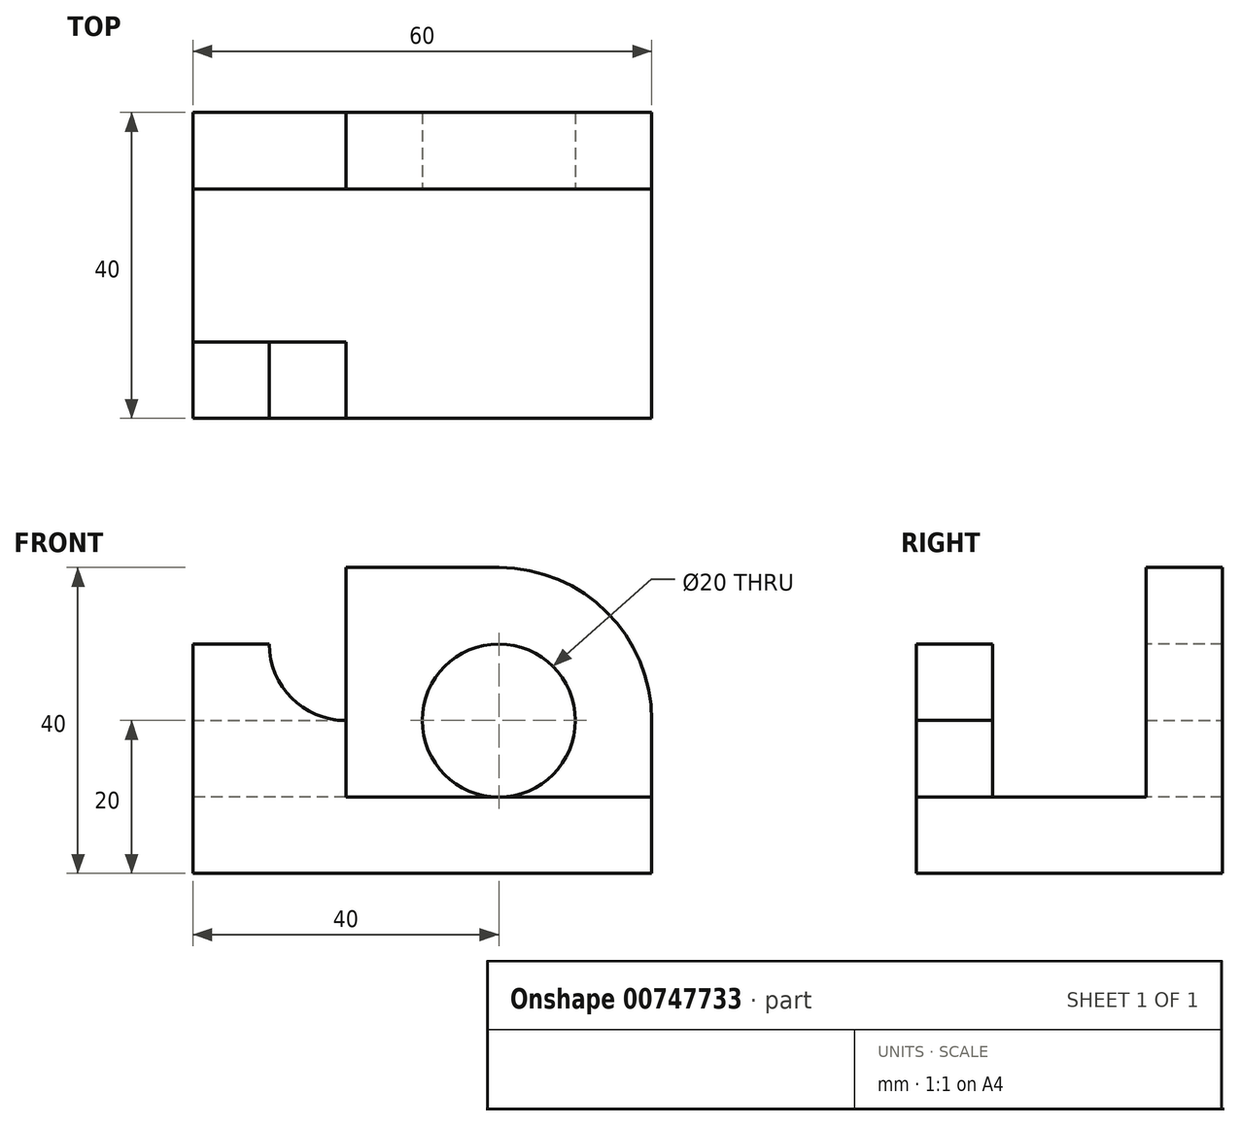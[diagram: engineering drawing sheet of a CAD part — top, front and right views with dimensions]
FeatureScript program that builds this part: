
annotation { "Feature Type Name" : "Feature", "Feature Type Description" : "" }
export const myFeature = defineFeature(function(context is Context, id is Id, definition is map)
    precondition{}
    {
        {
            var Q0;
            Q0=qCreatedBy(makeId("Top.planeOp"),FACE);
            var sketch = newSketch(context, id + "F0", { "sketchPlane" : qUnion([Q0])});
            skLineSegment(sketch, "E0", {"start": v(0, 0) * mm, "end": v(60, 0) * mm});
            skLineSegment(sketch, "E1", {"start": v(60, 0) * mm, "end": v(60, 40) * mm});
            skLineSegment(sketch, "E2", {"start": v(60, 40) * mm, "end": v(0, 40) * mm});
            skLineSegment(sketch, "E3", {"start": v(0, 40) * mm, "end": v(0, 0) * mm});
            skSolve(sketch);
        }
        {
            var Q0;
            Q0=qSketchRegion(id+"F0",true);
            extrude(context, id + "F1", {"entities" : qUnion([Q0]), "depth" : 40 * mm, "offsetDistance" : 25 * mm});
        }
        {
            var Q0;
            Q0=makeQuery(id+"F1.opExtrude","CAP_FACE",FACE,{"disambiguationData":[OSD([sQuery(id+"F0.wireOp",EDGE,"E0"),sQuery(id+"F0.wireOp",EDGE,"E1"),sQuery(id+"F0.wireOp",EDGE,"E2"),sQuery(id+"F0.wireOp",EDGE,"E3")])],"isStart":false});
            var sketch = newSketch(context, id + "F2", { "sketchPlane" : qUnion([Q0])});
            skLineSegment(sketch, "E4", {"start": v(0, 40) * mm, "end": v(0, 30) * mm});
            skLineSegment(sketch, "E5", {"start": v(0, 30) * mm, "end": v(0, 10) * mm});
            skLineSegment(sketch, "E6", {"start": v(0, 10) * mm, "end": v(60, 10) * mm});
            skLineSegment(sketch, "E7", {"start": v(60, 10) * mm, "end": v(60, 30) * mm});
            skLineSegment(sketch, "E8", {"start": v(60, 30) * mm, "end": v(0, 30) * mm});
            skLineSegment(sketch, "E9", {"start": v(0, 40) * mm, "end": v(20, 40) * mm});
            skLineSegment(sketch, "E10", {"start": v(20, 40) * mm, "end": v(20, 30) * mm});
            skLineSegment(sketch, "E11", {"start": v(20, 30) * mm, "end": v(0, 30) * mm});
            skSolve(sketch);
        }
        {
            var Q0;
            Q0=makeQuery(id+"F2.imprint","IMPRINT",FACE,{"disambiguationData":[TD([[makeQuery(id+"F2.imprint","IMPRINT",EDGE,{"derivedFrom":sQuery(id+"F2.wireOp",EDGE,"E4")}),1.0]])]});
            extrude(context, id + "F3", {"entities" : qUnion([Q0]), "operationType" : NewBodyOperationType.REMOVE, "oppositeDirection" : true, "depth" : 10 * mm, "offsetDistance" : 25 * mm});
        }
        {
            var Q0;
            Q0=makeQuery(id+"F2.imprint","IMPRINT",FACE,{"disambiguationData":[TD([[makeQuery(id+"F2.imprint","IMPRINT",EDGE,{"derivedFrom":sQuery(id+"F2.wireOp",EDGE,"E5")}),1.0]])]});
            extrude(context, id + "F4", {"entities" : qUnion([Q0]), "operationType" : NewBodyOperationType.REMOVE, "oppositeDirection" : true, "depth" : 30 * mm, "offsetDistance" : 25 * mm});
        }
        {
            var Q0;
            Q0=makeQuery(id+"F1.opExtrude","SWEPT_FACE",FACE,{"disambiguationData":[OSD([sQuery(id+"F0.wireOp",EDGE,"E0")])]});
            var sketch = newSketch(context, id + "F5", { "sketchPlane" : qUnion([Q0])});
            skLineSegment(sketch, "E12.bottom", {"start": v(0, 40) * mm, "end": v(60, 40) * mm});
            skLineSegment(sketch, "E12.top", {"start": v(0, 30) * mm, "end": v(60, 30) * mm});
            skLineSegment(sketch, "E12.left", {"start": v(0, 40) * mm, "end": v(0, 30) * mm});
            skLineSegment(sketch, "E12.right", {"start": v(60, 40) * mm, "end": v(60, 30) * mm});
            skSolve(sketch);
        }
        {
            var Q0;
            Q0=makeQuery(id+"F5.imprint","IMPRINT",FACE,{"disambiguationData":[TD([[makeQuery(id+"F5.imprint","IMPRINT",EDGE,{"derivedFrom":sQuery(id+"F5.wireOp",EDGE,"E12.bottom")}),-1.0]])]});
            extrude(context, id + "F6", {"entities" : qUnion([Q0]), "operationType" : NewBodyOperationType.REMOVE, "oppositeDirection" : true, "depth" : 10 * mm, "offsetDistance" : 25 * mm});
        }
        {
            var Q0;
            Q0=makeQuery(id+"F1.opExtrude","SWEPT_FACE",FACE,{"disambiguationData":[OSD([sQuery(id+"F0.wireOp",EDGE,"E0")])]});
            var sketch = newSketch(context, id + "F7", { "sketchPlane" : qUnion([Q0])});
            skLineSegment(sketch, "E13.bottom", {"start": v(60, 30) * mm, "end": v(20, 30) * mm});
            skLineSegment(sketch, "E13.top", {"start": v(60, 10) * mm, "end": v(20, 10) * mm});
            skLineSegment(sketch, "E13.left", {"start": v(60, 30) * mm, "end": v(60, 10) * mm});
            skLineSegment(sketch, "E13.right", {"start": v(20, 30) * mm, "end": v(20, 10) * mm});
            skSolve(sketch);
        }
        {
            var Q0;
            Q0=makeQuery(id+"F7.imprint","IMPRINT",FACE,{"disambiguationData":[TD([[makeQuery(id+"F7.imprint","IMPRINT",EDGE,{"derivedFrom":sQuery(id+"F7.wireOp",EDGE,"E13.bottom")}),-1.0]])]});
            extrude(context, id + "F8", {"entities" : qUnion([Q0]), "operationType" : NewBodyOperationType.REMOVE, "oppositeDirection" : true, "depth" : 10 * mm, "offsetDistance" : 25 * mm});
        }
        {
            var Q0;
            Q0=makeQuery(id+"F1.opExtrude","SWEPT_FACE",FACE,{"disambiguationData":[OSD([sQuery(id+"F0.wireOp",EDGE,"E0")])]});
            var sketch = newSketch(context, id + "F9", { "sketchPlane" : qUnion([Q0])});
            skLineSegment(sketch, "E14", {"start": v(20, 10) * mm, "end": v(20, 20) * mm});
            skLineSegment(sketch, "E15", {"start": v(20, 20) * mm, "end": v(10, 20) * mm});
            skLineSegment(sketch, "E16", {"start": v(10, 20) * mm, "end": v(10, 30) * mm});
            skArc(sketch, "E17", {"start": v(10, 30) * mm, "mid": v(12.93, 22.93) * mm, "end": v(20, 20) * mm});
            skSolve(sketch);
        }
        {
            var Q0;
            {var subQ0=sQuery(id+"F9.wireOp",EDGE,"E17");Q0=makeQuery(id+"F9.imprint","IMPRINT",FACE,{"disambiguationData":[TD([[makeQuery(id+"F9.imprint","IMPRINT",EDGE,{"derivedFrom":subQ0}),1.0]])]});}
            extrude(context, id + "F10", {"entities" : qUnion([Q0]), "operationType" : NewBodyOperationType.REMOVE, "oppositeDirection" : true, "depth" : 10 * mm, "offsetDistance" : 25 * mm});
        }
        {
            var Q0;
            Q0=makeQuery(id+"F1.opExtrude","SWEPT_FACE",FACE,{"disambiguationData":[OSD([sQuery(id+"F0.wireOp",EDGE,"E2")])]});
            var sketch = newSketch(context, id + "F11", { "sketchPlane" : qUnion([Q0])});
            skLineSegment(sketch, "E18.bottom", {"start": v(0, 30) * mm, "end": v(-20, 30) * mm});
            skLineSegment(sketch, "E18.top", {"start": v(0, 20) * mm, "end": v(-20, 20) * mm});
            skLineSegment(sketch, "E18.left", {"start": v(0, 30) * mm, "end": v(0, 20) * mm});
            skLineSegment(sketch, "E18.right", {"start": v(-20, 30) * mm, "end": v(-20, 20) * mm});
            skSolve(sketch);
        }
        {
            var Q0;
            Q0=qSketchRegion(id+"F11",true);
            extrude(context, id + "F12", {"entities" : qUnion([Q0]), "operationType" : NewBodyOperationType.REMOVE, "oppositeDirection" : true, "depth" : 10 * mm, "offsetDistance" : 25 * mm});
        }
        {
            var Q0;
            Q0=makeQuery(id+"F4.boolean.opBoolean","COPY",FACE,{"derivedFrom":makeQuery(id+"F4.opExtrude","SWEPT_FACE",FACE,{"disambiguationData":[OSD([sQuery(id+"F2.wireOp",EDGE,"E8"),sQuery(id+"F2.wireOp",EDGE,"E11")])]})});
            var sketch = newSketch(context, id + "F13", { "sketchPlane" : qUnion([Q0])});
            skLineSegment(sketch, "E19", {"start": v(60, 10) * mm, "end": v(60, 20) * mm});
            skLineSegment(sketch, "E20", {"start": v(60, 20) * mm, "end": v(40, 20) * mm});
            skLineSegment(sketch, "E21", {"start": v(40, 20) * mm, "end": v(20, 20) * mm});
            skCircle(sketch, "E22", {"center": v(40, 20) * mm, "radius": 10 * mm});
            skArc(sketch, "E23", {"start": v(60, 20) * mm, "mid": v(40, 40) * mm, "end": v(20, 20) * mm});
            skSolve(sketch);
        }
        {
            var Q0;
            {var subQ0=sQuery(id+"F13.wireOp",EDGE,"E21");var subQ1=sQuery(id+"F13.wireOp",EDGE,"E20");var subQ2=makeQuery(id+"F13.imprint","INTERSECT",VERTEX,{"derivedFrom":[subQ1,subQ0]});Q0=makeQuery(id+"F13.imprint","IMPRINT",FACE,{"disambiguationData":[TD([[makeQuery(id+"F13.imprint","IMPRINT",EDGE,{"disambiguationData":[TD([[subQ2,1.0]])],"derivedFrom":subQ1}),-1.0]])]});}
            var Q1;
            {var subQ0=sQuery(id+"F13.wireOp",EDGE,"E21");var subQ1=sQuery(id+"F13.wireOp",EDGE,"E20");var subQ2=makeQuery(id+"F13.imprint","INTERSECT",VERTEX,{"derivedFrom":[subQ1,subQ0]});Q1=makeQuery(id+"F13.imprint","IMPRINT",FACE,{"disambiguationData":[TD([[makeQuery(id+"F13.imprint","IMPRINT",EDGE,{"disambiguationData":[TD([[subQ2,1.0]])],"derivedFrom":subQ1}),1.0]])]});}
            var Q2;
            {var subQ0=sQuery(id+"F13.wireOp",EDGE,"E23");var subQ1=sQuery(id+"F2.wireOp",EDGE,"E8");var subQ4=makeQuery(id+"F4.boolean.opBoolean","COPY",EDGE,{"derivedFrom":makeQuery(id+"F4.opExtrude","CAP_EDGE",EDGE,{"disambiguationData":[OSD([subQ1,sQuery(id+"F2.wireOp",EDGE,"E11")])],"isStart":true})});var subQ5=makeQuery(id+"F13.imprint","INTERSECT",VERTEX,{"derivedFrom":[subQ4,subQ0]});Q2=makeQuery(id+"F13.imprint","IMPRINT",FACE,{"disambiguationData":[TD([[makeQuery(id+"F13.imprint","IMPRINT",EDGE,{"disambiguationData":[TD([[subQ5,1.0]])],"derivedFrom":subQ0}),-1.0]])]});}
            var Q3;
            {var subQ1=sQuery(id+"F2.wireOp",EDGE,"E11");var subQ2=sQuery(id+"F2.wireOp",EDGE,"E8");var subQ3=makeQuery(id+"F12.boolean.opBoolean","MERGE",EDGE,{"derivedFrom":[makeQuery(id+"F3.boolean.opBoolean","COPY",EDGE,{"derivedFrom":makeQuery(id+"F3.opExtrude","SWEPT_EDGE",EDGE,{"disambiguationData":[OSD([subQ2,sQuery(id+"F2.wireOp",EDGE,"E10"),subQ1])]})}),makeQuery(id+"F12.opExtrude","CAP_EDGE",EDGE,{"disambiguationData":[OSD([sQuery(id+"F11.wireOp",EDGE,"E18.right")])],"isStart":false})]});Q3=makeQuery(id+"F13.imprint","IMPRINT",FACE,{"disambiguationData":[TD([[makeQuery(id+"F13.imprint","IMPRINT",EDGE,{"derivedFrom":subQ3}),-1.0]])]});}
            extrude(context, id + "F14", {"entities" : qUnion([Q0, Q1, Q2, Q3]), "operationType" : NewBodyOperationType.REMOVE, "oppositeDirection" : true, "depth" : 10 * mm, "offsetDistance" : 25 * mm});
        }
    });
